# Revit family: Reception-Teknion-B_CWG_Main_Worksurface_with_Two_Gables_Reception_Desk-R2018
name_source: partatom
category: Furniture
revit_build: Autodesk Revit 2018 (Build: 20170223_1515(x64)
units: mm (PartAtom-declared; Revit-internal decimal feet)

## family parameters
Always vertical = Yes
Cut with Voids When Loaded = No
OmniClass Number = 23.40.20.00
OmniClass Title = General Furniture and Specialties
Room Calculation Point = No
Shared = Yes
Work Plane-Based = No

## types (6) — shared parameters
Assembly Code = E2020200
Manufacturer = Teknion
Manufacturer Fax = 416.661.4586
Part Number = B_CWG
Product Documentation Link = https://www.teknion.com
Product Line = Expansion Casegoods
Product Page URL = https://www.teknion.com
Series = Expansion Casegoods
Sustainability Data = https://www.teknion.com
URL = www.teknion.com
Unit Weight URL = http://www.teknion.com
Warranty = http://www.teknion.com

## per-type parameters (varying)
| type | Both Ends | Centered Grommet | Description | Gable Thickness | Model | Worksurface Thickness |
| 1" Worksurface Thickness, Centered Grommet Option | No | Yes | Main Worksurface with Two Gables - Reception Desk, 1" Worksurface Thickness, Centered Grommet Option | 1.016 " | BDCWG_____C | 1 " |
| 1 3/16" Worksurface Thickness, Centered Grommet Option | No | Yes | Main Worksurface with Two Gables - Reception Desk, 1 3/16" Worksurface Thickness, Centered Grommet Option | 1.016 " | BMCWG_____C | 1.189 " |
| 1 9/16" Worksurface Thickness, Centered Grommet Option | No | Yes | Main Worksurface with Two Gables - Reception Desk, 1 9/16" Worksurface Thickness, Centered Grommet Option | 1.512 " | BXCWG_____C | 1.555 " |
| 1" Worksurface Thickness, Both Ends Grommet Option | Yes | No | Main Worksurface with Two Gables - Reception Desk, 1" Worksurface Thickness, Both Ends Grommet Option | 1.016 " | BDCWG_____B | 1 " |
| 1 3/16" Worksurface Thickness, Both Ends Grommet Option | Yes | No | Main Worksurface with Two Gables - Reception Desk, 1 3/16" Worksurface Thickness, Both Ends Grommet Option | 1.016 " | BMCWG_____B | 1.189 " |
| 1 9/16" Worksurface Thickness, Both Ends Grommet Option | Yes | No | Main Worksurface with Two Gables - Reception Desk, 1 9/16" Worksurface Thickness, Both Ends Grommet Option | 1.512 " | BXCWG_____B | 1.555 " |

## geometry (parser evidence)
native form markers: Sweep x2
no freeform markers — native parametric forms only
